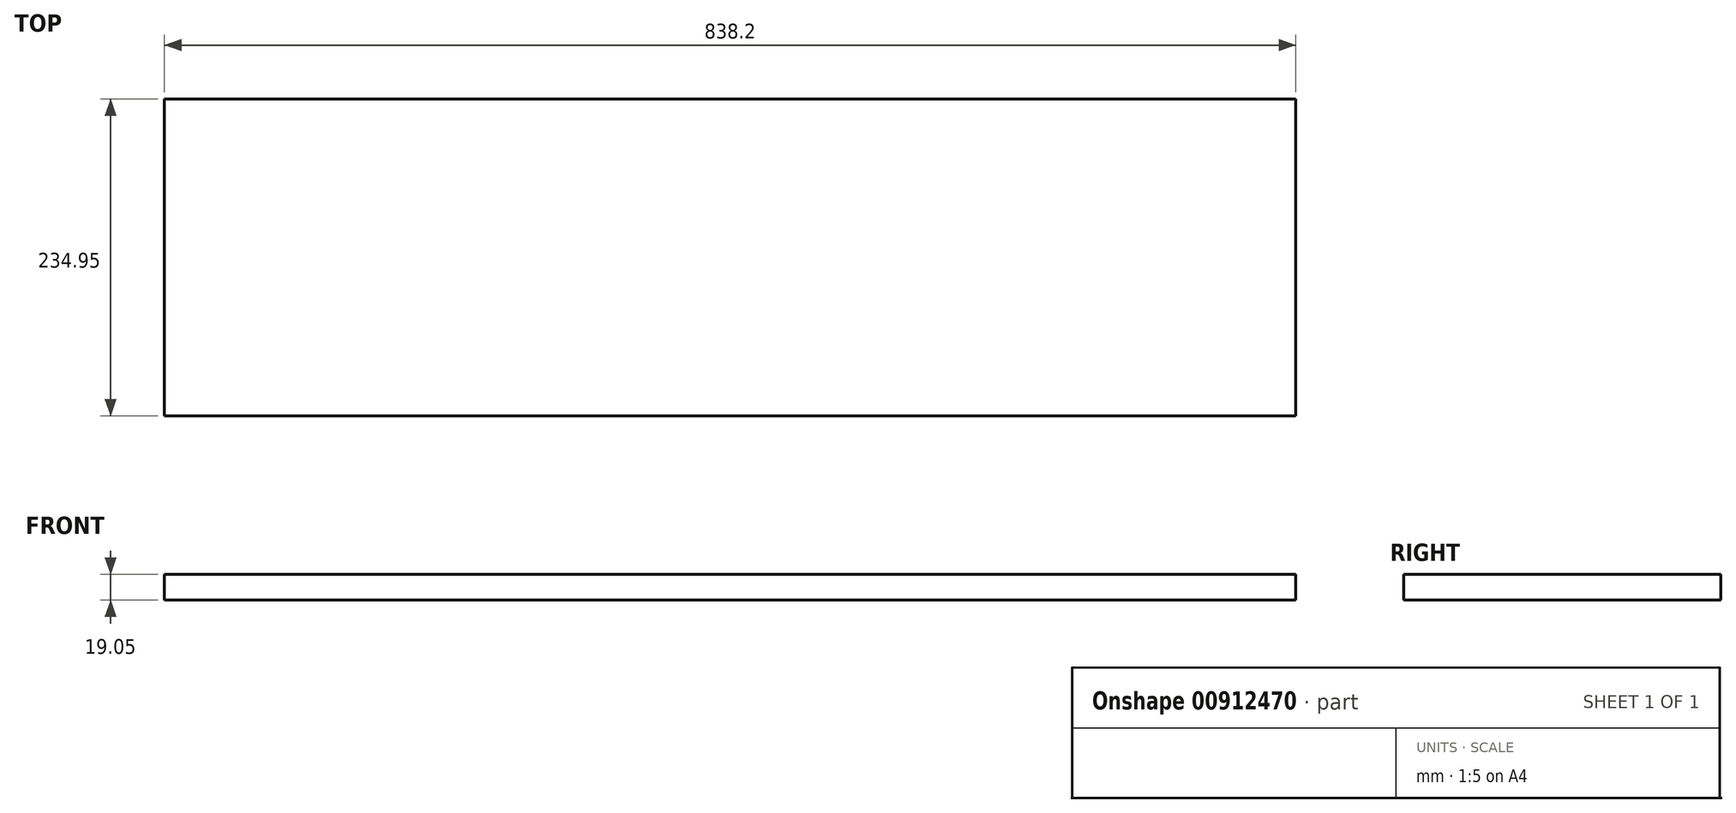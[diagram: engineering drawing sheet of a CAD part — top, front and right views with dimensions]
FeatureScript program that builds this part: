
annotation { "Feature Type Name" : "Feature", "Feature Type Description" : "" }
export const myFeature = defineFeature(function(context is Context, id is Id, definition is map)
    precondition{}
    {
        {
            var Q0;
            Q0=qCreatedBy(makeId("Right.planeOp"),FACE);
            var sketch = newSketch(context, id + "F0", { "sketchPlane" : qUnion([Q0])});
            skLineSegment(sketch, "E0.bottom", {"start": v(0, 0) * mm, "end": v(234.95, 0) * mm});
            skLineSegment(sketch, "E0.top", {"start": v(0, 19.05) * mm, "end": v(234.95, 19.05) * mm});
            skLineSegment(sketch, "E0.left", {"start": v(0, 0) * mm, "end": v(0, 19.05) * mm});
            skLineSegment(sketch, "E0.right", {"start": v(234.95, 0) * mm, "end": v(234.95, 19.05) * mm});
            skSolve(sketch);
        }
        {
            var Q0;
            Q0 = qSketchRegion(id + "F0", true);
            extrude(context, id + "F1", {"entities" : qUnion([Q0]), "depth" : 838.2 * mm, "offsetDistance" : 25.4 * mm});
        }
    });
